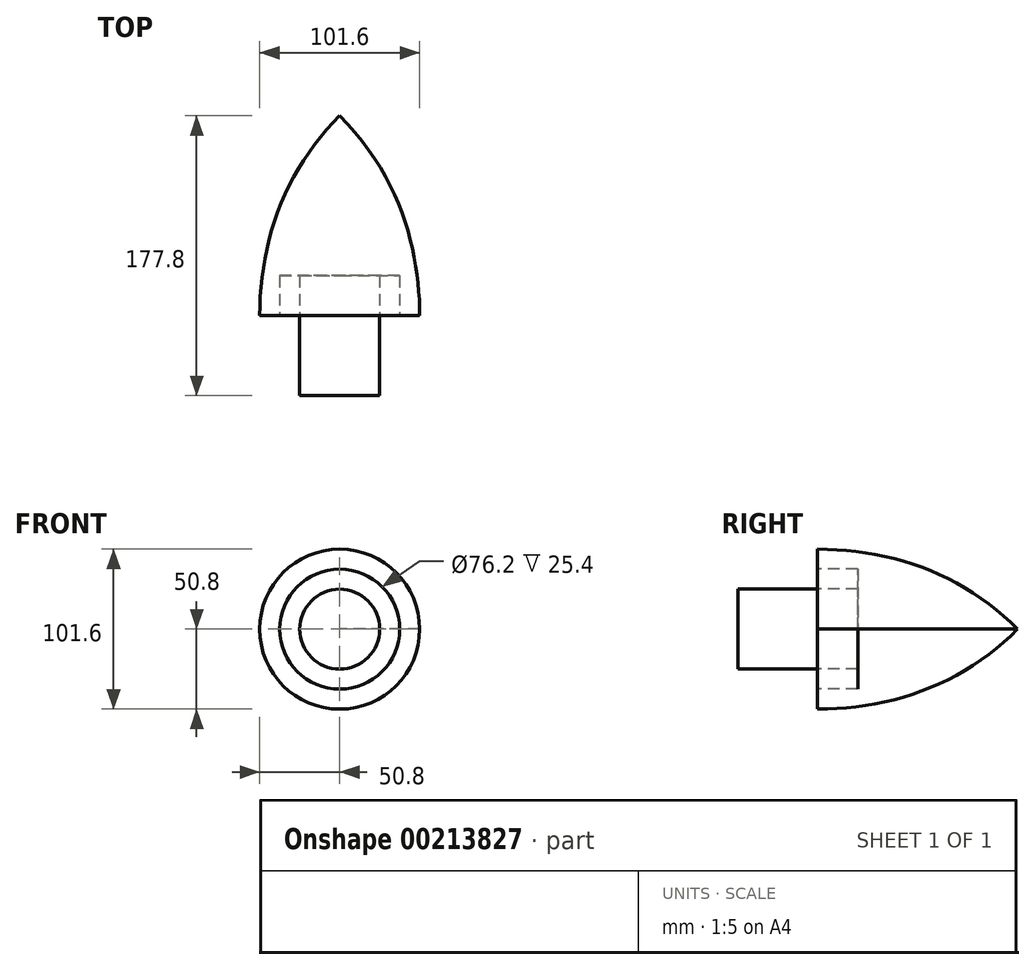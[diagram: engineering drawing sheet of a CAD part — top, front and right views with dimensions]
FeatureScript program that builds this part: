
annotation { "Feature Type Name" : "Feature", "Feature Type Description" : "" }
export const myFeature = defineFeature(function(context is Context, id is Id, definition is map)
    precondition{}
    {
        {
            var Q0;
            Q0=qCreatedBy(makeId("Top.planeOp"),FACE);
            var sketch = newSketch(context, id + "F0", { "sketchPlane" : qUnion([Q0])});
            skLineSegment(sketch, "E0", {"start": v(0, 127) * mm, "end": v(0, 0) * mm});
            skLineSegment(sketch, "E1", {"start": v(0, 0) * mm, "end": v(50.8, 0) * mm});
            skFitSpline(sketch, "E2", {"points": [v(50.8, 0) * mm, v(0, 127) * mm], "startDerivative": vector(0, 114.3) * mm, "endDerivative": vector(-120.93, 120.93) * mm});
            skLineSegment(sketch, "E3", {"start": v(0, 127) * mm, "end": v(71.69, 55.31) * mm, "construction": true});
            skSolve(sketch);
        }
        {
            var Q0;
            Q0=makeQuery(id+"F0.imprint","IMPRINT",FACE,{"disambiguationData":[TD([[makeQuery(id+"F0.imprint","IMPRINT",EDGE,{"derivedFrom":sQuery(id+"F0.wireOp",EDGE,"E0")}),1.0]])]});
            var Q1;
            Q1=sQuery(id+"F0.wireOp",EDGE,"E2");
            var Q2;
            Q2=sQuery(id+"F0.wireOp",EDGE,"E0");
            revolve(context, id + "F1", {"entities" : qUnion([Q0]), "surfaceEntities" : qUnion([Q1]), "axis" : qUnion([Q2]), "revolveType" : RevolveType.FULL});
        }
        {
            var Q0;
            Q0=makeQuery(id+"F1.opRevolve","SWEPT_FACE",FACE,{"disambiguationData":[OSD([sQuery(id+"F0.wireOp",EDGE,"E1")])]});
            var sketch = newSketch(context, id + "F2", { "sketchPlane" : qUnion([Q0])});
            skCircle(sketch, "E4", {"center": v(0, 0) * mm, "radius": 25.4 * mm});
            skCircle(sketch, "E5", {"center": v(0, 0) * mm, "radius": 38.1 * mm});
            skSolve(sketch);
        }
        {
            var Q0;
            Q0 = qSketchRegion(id + "F2", true);
            extrude(context, id + "F3", {"entities" : qUnion([Q0]), "operationType" : NewBodyOperationType.REMOVE, "oppositeDirection" : true, "depth" : 25.4 * mm});
        }
        {
            var Q0;
            Q0=makeQuery(id+"F2.imprint","IMPRINT",FACE,{"disambiguationData":[TD([[makeQuery(id+"F2.imprint","IMPRINT",EDGE,{"derivedFrom":sQuery(id+"F2.wireOp",EDGE,"E4")}),1.0]])]});
            extrude(context, id + "F4", {"entities" : qUnion([Q0]), "operationType" : NewBodyOperationType.ADD, "depth" : 50.8 * mm});
        }
    });
